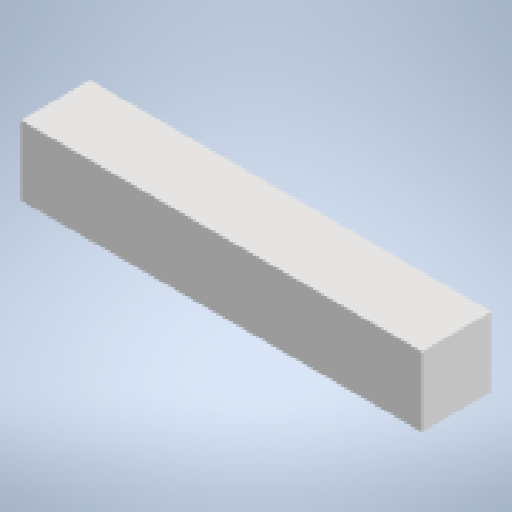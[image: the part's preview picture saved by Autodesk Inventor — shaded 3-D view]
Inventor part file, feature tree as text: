
AUTODESK INVENTOR PART (.ipt)
format: ipt  version: 2024 (Build 280153000, 153)  size: 124,928 bytes
history: native  units: mm
features: extrude x1, sketch x1
ambient origin geometry x8: Origin, YZ Plane, XZ Plane, XY Plane, X Axis, Y Axis, Z Axis, Center Point
bodies: Solid1 (feature_tree)
feature tree (2):
  extrude  "Extrusion1"  Depth=45.0mm
  sketch  "Sketch2"  dims[d0=45.0mm d1=45.0mm d2=260.0mm d3=0.0mm]
